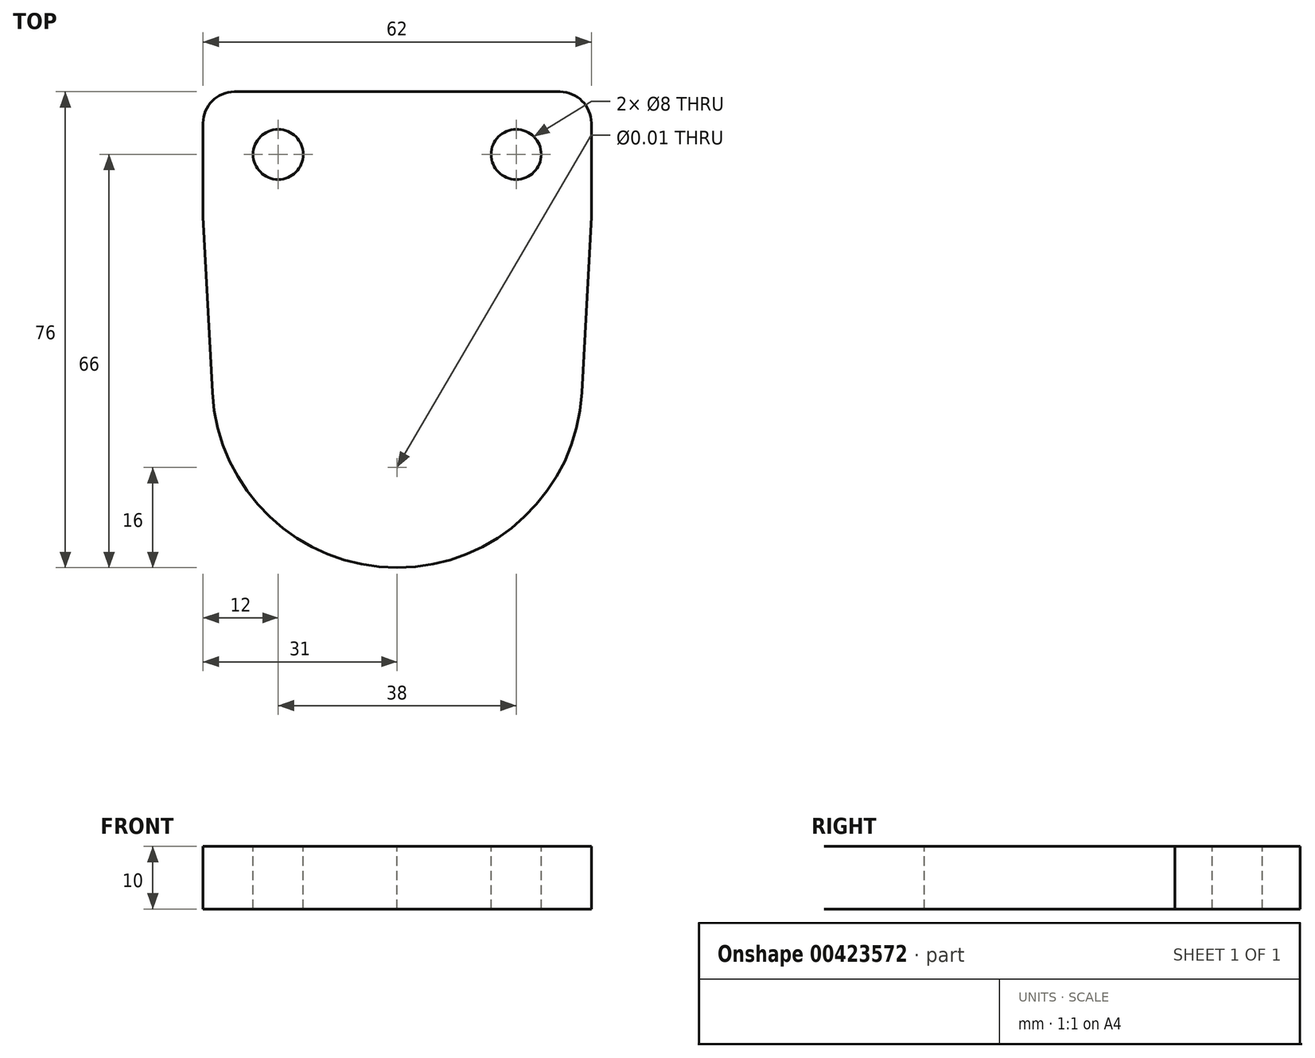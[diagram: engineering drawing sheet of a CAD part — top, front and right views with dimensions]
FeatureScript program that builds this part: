
annotation { "Feature Type Name" : "Feature", "Feature Type Description" : "" }
export const myFeature = defineFeature(function(context is Context, id is Id, definition is map)
    precondition{}
    {
        {
            var Q0;
            Q0=qCreatedBy(makeId("Top.planeOp"),FACE);
            var sketch = newSketch(context, id + "F0", { "sketchPlane" : qUnion([Q0])});
            skLineSegment(sketch, "E0.bottom", {"start": v(28, -38) * mm, "end": v(-28, -38) * mm});
            skLineSegment(sketch, "E0.top", {"start": v(28, 38) * mm, "end": v(-28, 38) * mm});
            skLineSegment(sketch, "E0.left", {"start": v(28, -38) * mm, "end": v(28, 38) * mm});
            skLineSegment(sketch, "E0.right", {"start": v(-28, -38) * mm, "end": v(-28, 38) * mm});
            skPoint(sketch, "E0.middle", {"position": v(0, 0) * mm});
            skPoint(sketch, "E1", {"position": v(0, -22) * mm});
            skPoint(sketch, "E1.positionSnap0", {"position": v(0, -38) * mm});
            skPoint(sketch, "E2", {"position": v(-19, 28) * mm});
            skPoint(sketch, "E3", {"position": v(19, 28) * mm});
            skPoint(sketch, "E4", {"position": v(0, -10) * mm});
            skLineSegment(sketch, "E5", {"start": v(-28, 38) * mm, "end": v(-31, 38) * mm});
            skLineSegment(sketch, "E6", {"start": v(28, 38) * mm, "end": v(31, 38) * mm});
            skLineSegment(sketch, "E7", {"start": v(31, 38) * mm, "end": v(31, 18) * mm});
            skLineSegment(sketch, "E8", {"start": v(31, 18) * mm, "end": v(28, -38) * mm});
            skLineSegment(sketch, "E9", {"start": v(-31, 38) * mm, "end": v(-31, 18) * mm});
            skLineSegment(sketch, "E10", {"start": v(-31, 18) * mm, "end": v(-28, -38) * mm});
            skSolve(sketch);
        }
        {
            var Q0;
            Q0=makeQuery(id+"F0.imprint","IMPRINT",FACE,{"disambiguationData":[TD([[makeQuery(id+"F0.imprint","IMPRINT",EDGE,{"derivedFrom":sQuery(id+"F0.wireOp",EDGE,"E0.bottom")}),-1.0]])]});
            var Q1;
            {var subQ0=sQuery(id+"F0.wireOp",EDGE,"E5");Q1=makeQuery(id+"F0.imprint","IMPRINT",FACE,{"disambiguationData":[TD([[makeQuery(id+"F0.imprint","IMPRINT",EDGE,{"derivedFrom":subQ0}),1.0]])]});}
            var Q2;
            {var subQ0=sQuery(id+"F0.wireOp",EDGE,"E6");Q2=makeQuery(id+"F0.imprint","IMPRINT",FACE,{"disambiguationData":[TD([[makeQuery(id+"F0.imprint","IMPRINT",EDGE,{"derivedFrom":subQ0}),-1.0]])]});}
            extrude(context, id + "F1", {"entities" : qUnion([Q0, Q1, Q2]), "oppositeDirection" : true, "depth" : 10 * mm});
        }
        {
            var Q0;
            Q0=sQuery(id+"F0.wireOp",VERTEX,"E1");
            var Q1;
            Q1=makeQuery(id+"F1.opExtrude","SWEPT_BODY",BODY,{"disambiguationData":[OSD([sQuery(id+"F0.wireOp",EDGE,"E0.bottom"),sQuery(id+"F0.wireOp",EDGE,"E0.top"),sQuery(id+"F0.wireOp",EDGE,"E0.left"),sQuery(id+"F0.wireOp",EDGE,"E0.right")])]});
            hole(context, id + "F2", {"style" : HoleStyle.SIMPLE, "endStyle" : HoleEndStyle.THROUGH, "standardTappedOrClearance" : lookupTablePath({ "standard" : "ANSI", "size" : "3/8 (0.38)", "type" : "Drilled" }), "standardBlindInLast" : lookupTablePath({ "standard" : "ANSI", "size" : "3/8", "type" : "Drilled" }), "holeDiameter" : 3 / 203.2 * mm, "isTappedThrough" : true, "tappedDepth" : 12 * mm, "tapClearance" : 3, "locations" : qUnion([Q0]), "scope" : qUnion([Q1])});
        }
        {
            var Q0;
            Q0=makeQuery(id+"F1.opExtrude","SWEPT_EDGE",EDGE,{"disambiguationData":[OSD([sQuery(id+"F0.wireOp",EDGE,"E0.bottom"),sQuery(id+"F0.wireOp",EDGE,"E0.left")])]});
            var Q1;
            Q1=makeQuery(id+"F1.opExtrude","SWEPT_EDGE",EDGE,{"disambiguationData":[OSD([sQuery(id+"F0.wireOp",EDGE,"E0.bottom"),sQuery(id+"F0.wireOp",EDGE,"E0.right")])]});
            fillet(context, id + "F3", {"entities" : qUnion([Q0, Q1]), "radius" : 29.58 * mm, "tangentPropagation" : true, "allowEdgeOverflow" : false});
        }
        {
            var Q0;
            Q0=makeQuery(id+"F1.opExtrude","SWEPT_EDGE",EDGE,{"disambiguationData":[OSD([sQuery(id+"F0.wireOp",EDGE,"E5"),sQuery(id+"F0.wireOp",EDGE,"tIwCPceW-qZrQ-Ak2Z-8EJJ-6HYQrhkvcbjL")])]});
            var Q1;
            Q1=makeQuery(id+"F1.opExtrude","SWEPT_EDGE",EDGE,{"disambiguationData":[OSD([sQuery(id+"F0.wireOp",EDGE,"E6"),sQuery(id+"F0.wireOp",EDGE,"bnC0pVRT-66CC-ebjM-7mrn-D4dZiSPCAhaA")])]});
            fillet(context, id + "F4", {"entities" : qUnion([Q0, Q1]), "radius" : 5 * mm, "tangentPropagation" : true, "allowEdgeOverflow" : false});
        }
        {
            var Q0;
            Q0=sQuery(id+"F0.wireOp",VERTEX,"E2");
            var Q1;
            Q1=sQuery(id+"F0.wireOp",VERTEX,"E3");
            var Q2;
            Q2=makeQuery(id+"F1.opExtrude","SWEPT_BODY",BODY,{"disambiguationData":[OSD([sQuery(id+"F0.wireOp",EDGE,"E0.bottom"),sQuery(id+"F0.wireOp",EDGE,"E0.top"),sQuery(id+"F0.wireOp",EDGE,"E0.left"),sQuery(id+"F0.wireOp",EDGE,"E0.right")])]});
            hole(context, id + "F5", {"style" : HoleStyle.SIMPLE, "endStyle" : HoleEndStyle.THROUGH, "standardTappedOrClearance" : lookupTablePath({ "standard" : "ISO", "size" : "8", "type" : "Drilled" }), "standardBlindInLast" : lookupTablePath({ "standard" : "ISO", "size" : "8", "type" : "Drilled" }), "holeDiameter" : 8 * mm, "isTappedThrough" : true, "tappedDepth" : 12 * mm, "tapClearance" : 3, "locations" : qUnion([Q0, Q1]), "scope" : qUnion([Q2])});
        }
    });
